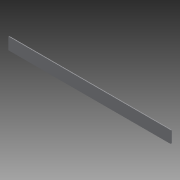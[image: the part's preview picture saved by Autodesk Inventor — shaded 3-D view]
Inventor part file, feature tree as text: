
AUTODESK INVENTOR PART (.ipt)
format: ipt  version: 2014 SP1 (Build 180222100, 222)  size: 76,800 bytes
history: native  units: in
note: dims shown in document units (in); Inventor stores cm internally (conversion verified against a paired STEP export)
features: extrude x1, fillet x1, sketch x1
ambient origin geometry x8: Origin, YZ Plane, XZ Plane, XY Plane, X Axis, Y Axis, Z Axis, Center Point
bodies: Solid1 (feature_tree)
feature tree (3):
  extrude  "Extrusion1"  Depth=27.0in
  fillet  "Fillet1"  Radius=0.125in
  sketch  "Sketch1"  dims[d0=2.0in d1=27.0in d2=0.125in d3=0.0in d4=0.125in]
